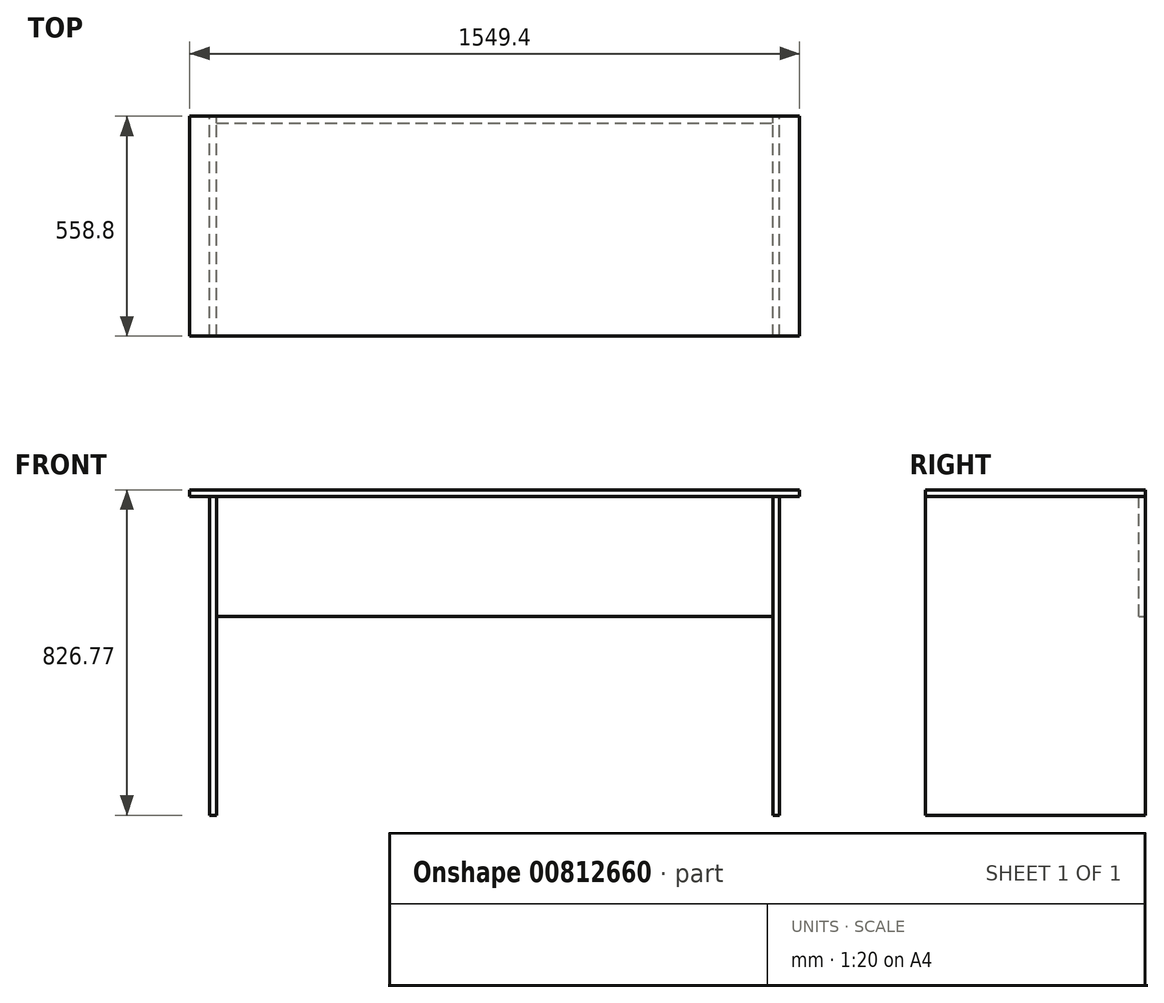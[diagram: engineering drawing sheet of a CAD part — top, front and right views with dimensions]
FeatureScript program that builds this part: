
annotation { "Feature Type Name" : "Feature", "Feature Type Description" : "" }
export const myFeature = defineFeature(function(context is Context, id is Id, definition is map)
    precondition{}
    {
        {
            var Q0;
            Q0=qCreatedBy(makeId("Front.planeOp"),FACE);
            var sketch = newSketch(context, id + "F0", { "sketchPlane" : qUnion([Q0])});
            skLineSegment(sketch, "E0.bottom", {"start": v(0, 0) * mm, "end": v(17.15, 0) * mm});
            skLineSegment(sketch, "E0.top", {"start": v(-50.8, 809.62) * mm, "end": v(0, 809.62) * mm});
            skLineSegment(sketch, "E0.left", {"start": v(0, 0) * mm, "end": v(0, 809.62) * mm});
            skLineSegment(sketch, "E0.right", {"start": v(17.15, 0) * mm, "end": v(17.14, 809.62) * mm});
            skLineSegment(sketch, "E1.bottom", {"start": v(0, 809.62) * mm, "end": v(1498.6, 809.62) * mm});
            skLineSegment(sketch, "E1.top", {"start": v(-50.8, 826.77) * mm, "end": v(1498.6, 826.77) * mm});
            skLineSegment(sketch, "E2.bottom", {"start": v(1447.8, 809.62) * mm, "end": v(1430.65, 809.62) * mm});
            skLineSegment(sketch, "E2.top", {"start": v(1447.8, 0) * mm, "end": v(1430.66, 0) * mm});
            skLineSegment(sketch, "E2.left", {"start": v(1447.8, 809.63) * mm, "end": v(1447.8, 0) * mm});
            skLineSegment(sketch, "E2.right", {"start": v(1430.65, 809.63) * mm, "end": v(1430.66, 0) * mm});
            skLineSegment(sketch, "E3.bottom", {"start": v(17.14, 809.62) * mm, "end": v(1430.65, 809.62) * mm});
            skLineSegment(sketch, "E3.top", {"start": v(17.14, 504.83) * mm, "end": v(1430.65, 504.83) * mm});
            skLineSegment(sketch, "E3.left", {"start": v(17.14, 809.62) * mm, "end": v(17.14, 504.83) * mm});
            skLineSegment(sketch, "E3.right", {"start": v(1430.65, 809.63) * mm, "end": v(1430.65, 504.83) * mm});
            skLineSegment(sketch, "E4.0", {"start": v(-50.8, 809.62) * mm, "end": v(-50.8, 826.77) * mm});
            skLineSegment(sketch, "E5.0", {"start": v(1498.6, 809.63) * mm, "end": v(1498.6, 826.77) * mm});
            skSolve(sketch);
        }
        {
            var Q0;
            {var subQ4=sQuery(id+"F0.wireOp",EDGE,"E0.bottom");Q0=makeQuery(id+"F0.imprint","IMPRINT",FACE,{"disambiguationData":[TD([[makeQuery(id+"F0.imprint","IMPRINT",EDGE,{"derivedFrom":subQ4}),1.0]])]});}
            extrude(context, id + "F1", {"entities" : qUnion([Q0]), "depth" : 558.8 * mm, "offsetDistance" : 25.4 * mm});
        }
        {
            var Q0;
            {var subQ5=sQuery(id+"F0.wireOp",EDGE,"E0.top");Q0=makeQuery(id+"F0.imprint","IMPRINT",FACE,{"disambiguationData":[TD([[makeQuery(id+"F0.imprint","IMPRINT",EDGE,{"derivedFrom":subQ5}),1.0]])]});}
            extrude(context, id + "F2", {"entities" : qUnion([Q0]), "depth" : 558.8 * mm, "offsetDistance" : 25.4 * mm});
        }
        {
            var Q0;
            {var subQ1=sQuery(id+"F0.wireOp",EDGE,"E2.top");Q0=makeQuery(id+"F0.imprint","IMPRINT",FACE,{"disambiguationData":[TD([[makeQuery(id+"F0.imprint","IMPRINT",EDGE,{"derivedFrom":subQ1}),-1.0]])]});}
            extrude(context, id + "F3", {"entities" : qUnion([Q0]), "depth" : 558.8 * mm, "offsetDistance" : 25.4 * mm});
        }
        {
            var Q0;
            {var subQ3=sQuery(id+"F0.wireOp",EDGE,"E3.top");Q0=makeQuery(id+"F0.imprint","IMPRINT",FACE,{"disambiguationData":[TD([[makeQuery(id+"F0.imprint","IMPRINT",EDGE,{"derivedFrom":subQ3}),1.0]])]});}
            extrude(context, id + "F4", {"entities" : qUnion([Q0]), "depth" : 17.14 * mm, "offsetDistance" : 25.4 * mm});
        }
    });
